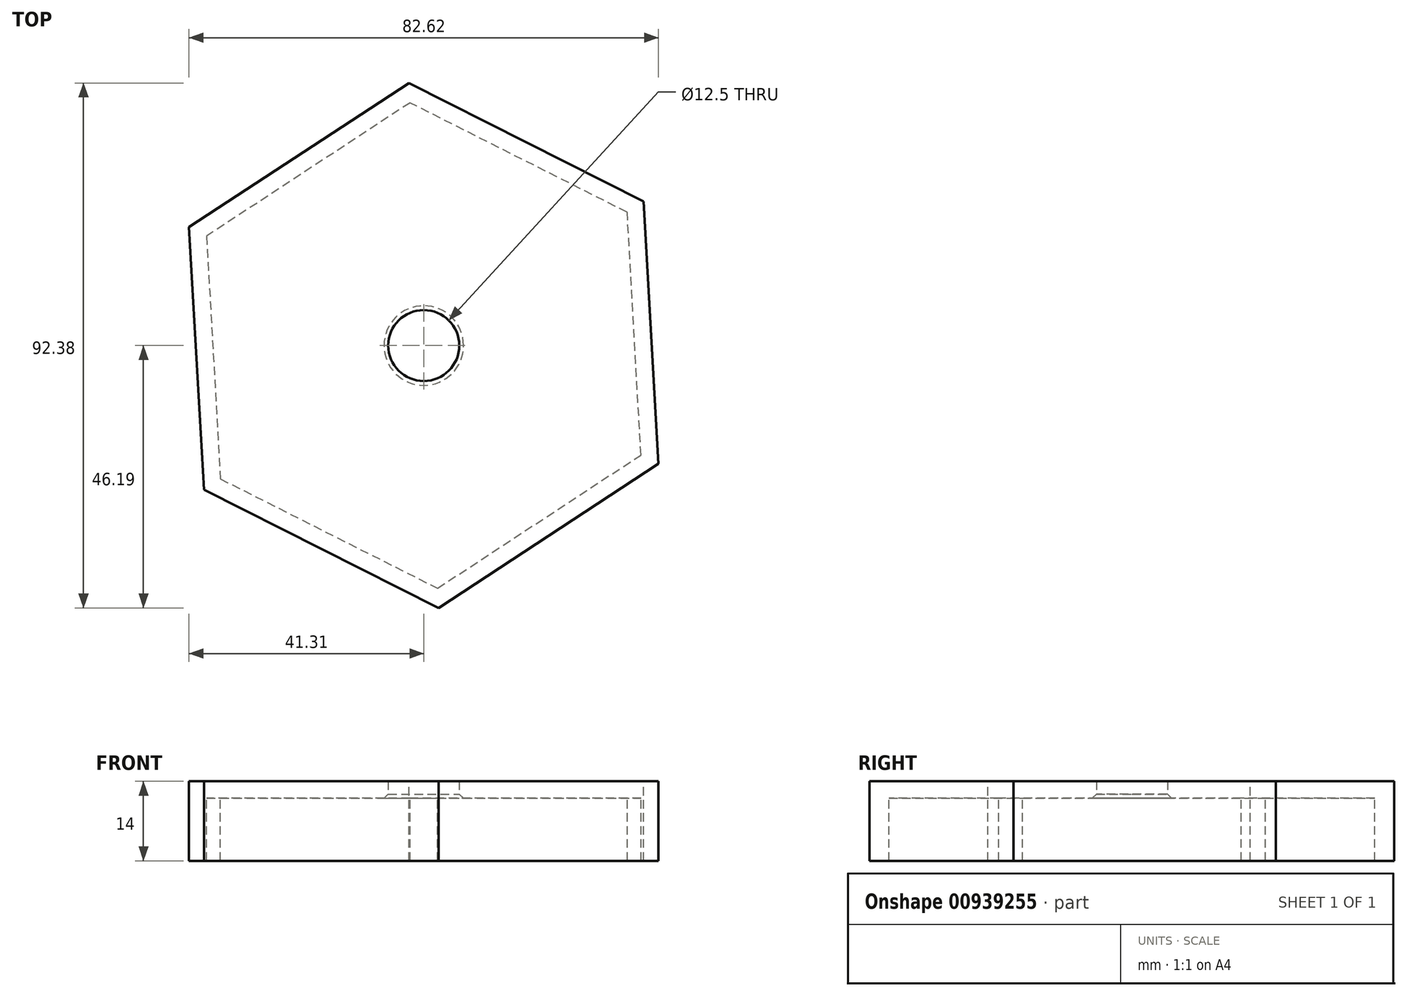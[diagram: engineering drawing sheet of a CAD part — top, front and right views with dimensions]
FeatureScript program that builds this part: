
annotation { "Feature Type Name" : "Feature", "Feature Type Description" : "" }
export const myFeature = defineFeature(function(context is Context, id is Id, definition is map)
    precondition{}
    {
        {
            var Q0;
            Q0=qCreatedBy(makeId("Top.planeOp"),FACE);
            var sketch = newSketch(context, id + "F0", { "sketchPlane" : qUnion([Q0])});
            skCircle(sketch, "E0.cCircle", {"center": v(0, 0) * mm, "radius": 40.06 * mm, "construction": true});
            skLineSegment(sketch, "E0.0", {"start": v(41.3, -20.83) * mm, "end": v(2.62, -46.19) * mm});
            skLineSegment(sketch, "E0.1", {"start": v(2.62, -46.19) * mm, "end": v(-38.7, -25.36) * mm});
            skLineSegment(sketch, "E0.2", {"start": v(-38.7, -25.36) * mm, "end": v(-41.3, 20.83) * mm});
            skLineSegment(sketch, "E0.3", {"start": v(-41.3, 20.83) * mm, "end": v(-2.62, 46.19) * mm});
            skLineSegment(sketch, "E0.4", {"start": v(-2.62, 46.19) * mm, "end": v(38.7, 25.36) * mm});
            skLineSegment(sketch, "E0.5", {"start": v(38.7, 25.36) * mm, "end": v(41.3, -20.83) * mm});
            skPoint(sketch, "E0.0.midPoint", {"position": v(21.96, -33.5) * mm});
            skSolve(sketch);
        }
        {
            var Q0;
            Q0=qCreatedBy(makeId("Front.planeOp"),FACE);
            var sketch = newSketch(context, id + "F1", { "sketchPlane" : qUnion([Q0])});
            skLineSegment(sketch, "E1", {"start": v(0, 0) * mm, "end": v(0, 14) * mm});
            skSolve(sketch);
        }
        {
            var Q0;
            Q0=makeQuery(id+"F0.imprint","IMPRINT",FACE,{"disambiguationData":[TD([[makeQuery(id+"F0.imprint","IMPRINT",EDGE,{"derivedFrom":sQuery(id+"F0.wireOp",EDGE,"E0.0")}),-1.0]])]});
            var Q1;
            Q1=sQuery(id+"F1.wireOp",EDGE,"E1");
            sweep(context, id + "F2", {"profiles" : qUnion([Q0]), "path" : qUnion([Q1])});
        }
        {
            var Q0;
            Q0=qCreatedBy(makeId("Top.planeOp"),FACE);
            var sketch = newSketch(context, id + "F3", { "sketchPlane" : qUnion([Q0])});
            skCircle(sketch, "E2", {"center": v(0, 0) * mm, "radius": 20 * mm});
            skSolve(sketch);
        }
        {
            var Q0;
            Q0=makeQuery(id+"F2.opSweep","CAP_FACE",FACE,{"disambiguationData":[OSD([sQuery(id+"F0.wireOp",EDGE,"E0.0"),sQuery(id+"F0.wireOp",EDGE,"E0.1"),sQuery(id+"F0.wireOp",EDGE,"E0.2"),sQuery(id+"F0.wireOp",EDGE,"E0.3"),sQuery(id+"F0.wireOp",EDGE,"E0.4"),sQuery(id+"F0.wireOp",EDGE,"E0.5"),sQuery(id+"F1.wireOp",VERTEX,"E1.start")])],"isStart":true});
            shell(context, id + "F4", {"entities" : qUnion([Q0]), "thickness" : 3 * mm});
        }
        {
            var Q0;
            Q0=sQuery(id+"F3.wireOp",VERTEX,"E2.center");
            var Q1;
            Q1=makeQuery(id+"F2.opSweep","SWEPT_BODY",BODY,{"disambiguationData":[OSD([sQuery(id+"F0.wireOp",EDGE,"E0.0"),sQuery(id+"F0.wireOp",EDGE,"E0.1"),sQuery(id+"F0.wireOp",EDGE,"E0.2"),sQuery(id+"F0.wireOp",EDGE,"E0.3"),sQuery(id+"F0.wireOp",EDGE,"E0.4"),sQuery(id+"F0.wireOp",EDGE,"E0.5"),sQuery(id+"F1.wireOp",EDGE,"E1")])]});
            hole(context, id + "F5", {"style" : HoleStyle.C_SINK, "endStyle" : HoleEndStyle.BLIND, "oppositeDirection" : true, "holeDiameter" : 12.5 * mm, "cSinkDiameter" : 14 * mm, "cSinkAngle" : 90 * degree, "majorDiameter" : 5 * mm, "holeDepth" : 5 * mm, "isTappedThrough" : true, "tappedDepth" : 4 * mm, "tapClearance" : 3, "locations" : qUnion([Q0]), "scope" : qUnion([Q1])});
        }
    });
